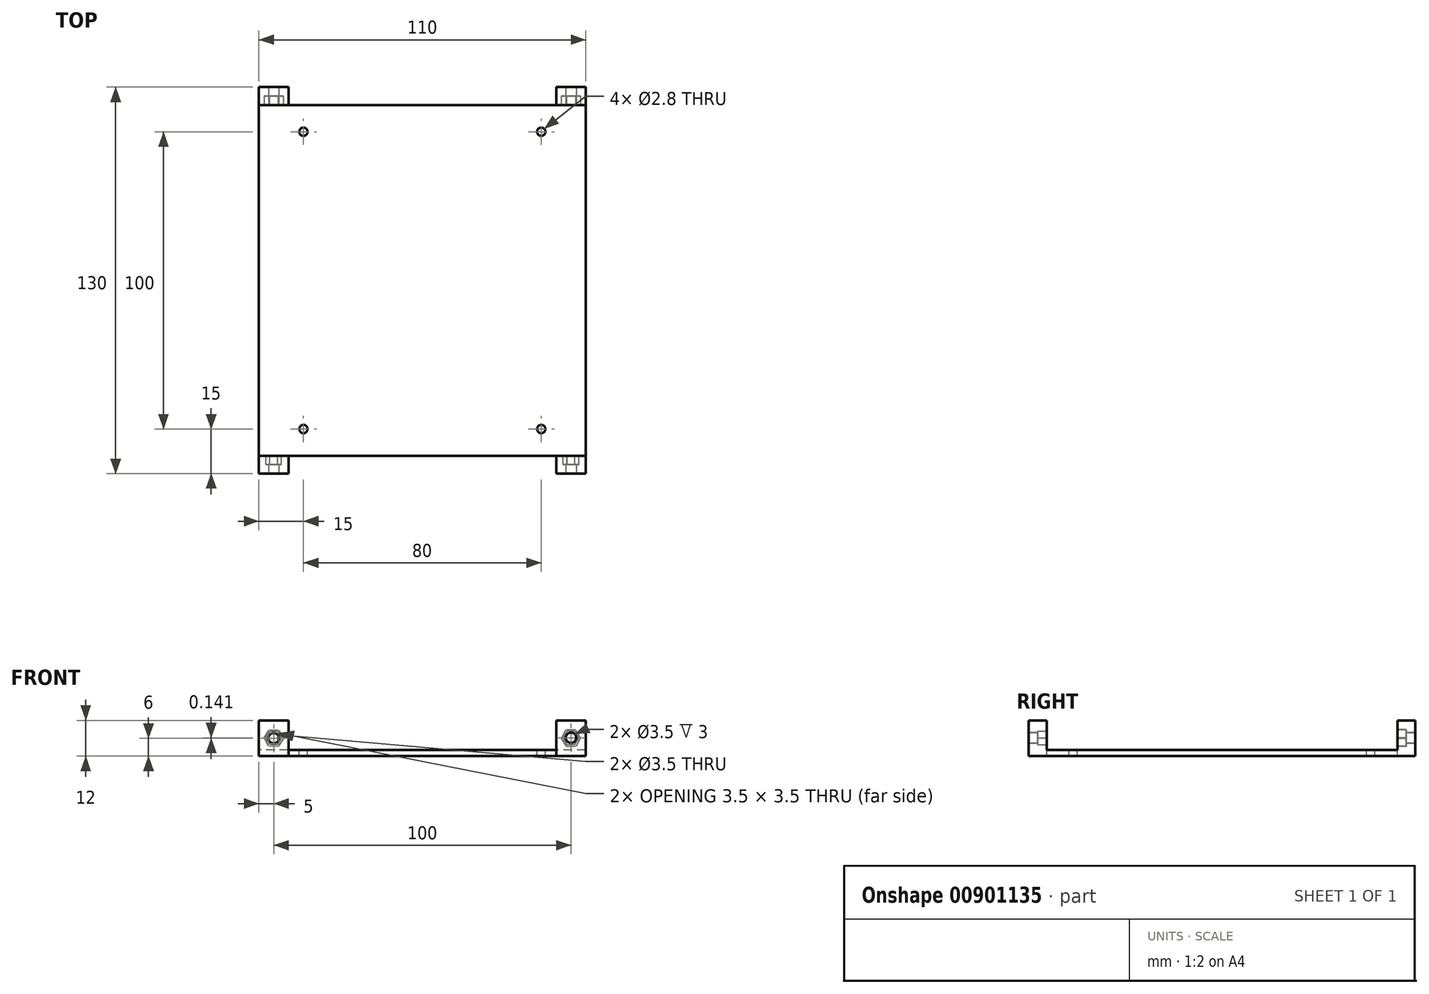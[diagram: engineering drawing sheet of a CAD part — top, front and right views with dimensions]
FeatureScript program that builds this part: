
annotation { "Feature Type Name" : "Feature", "Feature Type Description" : "" }
export const myFeature = defineFeature(function(context is Context, id is Id, definition is map)
    precondition{}
    {
        {
            var Q0;
            Q0=qCreatedBy(makeId("Right.planeOp"),FACE);
            var sketch = newSketch(context, id + "F0", { "sketchPlane" : qUnion([Q0])});
            skLineSegment(sketch, "E0.bottom", {"start": v(0, 25.4) * mm, "end": v(-59, 25.4) * mm});
            skLineSegment(sketch, "E0.top", {"start": v(0, 23.4) * mm, "end": v(-65, 23.4) * mm});
            skPoint(sketch, "E0.middle", {"position": v(0, 0) * mm});
            skLineSegment(sketch, "E1.top", {"start": v(-65, 35.4) * mm, "end": v(-59, 35.4) * mm});
            skLineSegment(sketch, "E1.right", {"start": v(-59, 25.4) * mm, "end": v(-59, 35.4) * mm});
            skLineSegment(sketch, "E2", {"start": v(0, 25.4) * mm, "end": v(0, 23.4) * mm, "construction": true});
            skLineSegment(sketch, "E3", {"start": v(-65, 35.4) * mm, "end": v(-65, 23.4) * mm});
            skLineSegment(sketch, "E4.MirrorCS", {"start": v(65, 35.4) * mm, "end": v(59, 35.4) * mm});
            skLineSegment(sketch, "E5.MirrorCS", {"start": v(0, 25.4) * mm, "end": v(59, 25.4) * mm});
            skLineSegment(sketch, "E6.MirrorCS", {"start": v(0, 23.4) * mm, "end": v(65, 23.4) * mm});
            skLineSegment(sketch, "E7.MirrorCS", {"start": v(59, 25.4) * mm, "end": v(59, 35.4) * mm});
            skLineSegment(sketch, "E8.MirrorCS", {"start": v(65, 35.4) * mm, "end": v(65, 23.4) * mm});
            skSolve(sketch);
        }
        {
            var Q0;
            Q0 = qSketchRegion(id + "F0", true);
            extrude(context, id + "F1", {"entities" : qUnion([Q0]), "endBound" : BoundingType.SYMMETRIC, "depth" : 110 * mm, "offsetDistance" : 25 * mm});
        }
        {
            var Q0;
            Q0=makeQuery(id+"F1.opExtrude","SWEPT_FACE",FACE,{"disambiguationData":[OSD([sQuery(id+"F0.wireOp",EDGE,"E4.MirrorCS")])]});
            var sketch = newSketch(context, id + "F2", { "sketchPlane" : qUnion([Q0])});
            skLineSegment(sketch, "E9.bottom", {"start": v(-45, 65) * mm, "end": v(45, 65) * mm});
            skLineSegment(sketch, "E9.top", {"start": v(-45, 59) * mm, "end": v(45, 59) * mm});
            skLineSegment(sketch, "E9.left", {"start": v(-45, 65) * mm, "end": v(-45, 59) * mm});
            skLineSegment(sketch, "E9.right", {"start": v(45, 65) * mm, "end": v(45, 59) * mm});
            skLineSegment(sketch, "E10.bottom", {"start": v(-45, -59) * mm, "end": v(45, -59) * mm});
            skLineSegment(sketch, "E10.top", {"start": v(-45, -65) * mm, "end": v(45, -65) * mm});
            skLineSegment(sketch, "E10.left", {"start": v(-45, -59) * mm, "end": v(-45, -65) * mm});
            skLineSegment(sketch, "E10.right", {"start": v(45, -59) * mm, "end": v(45, -65) * mm});
            skLineSegment(sketch, "E11", {"start": v(0, 89.7) * mm, "end": v(0, -84.78) * mm, "construction": true});
            skSolve(sketch);
        }
        {
            var Q0;
            Q0 = qSketchRegion(id + "F2", true);
            extrude(context, id + "F3", {"entities" : qUnion([Q0]), "operationType" : NewBodyOperationType.REMOVE, "oppositeDirection" : true, "depth" : 25 * mm, "offsetDistance" : 25 * mm});
        }
        {
            var Q0;
            {var subQ1=sQuery(id+"F0.wireOp",EDGE,"E3");Q0=makeQuery(id+"F3.boolean.opBoolean","SPLIT",FACE,{"disambiguationData":[TD([makeQuery(id+"F3.opExtrude","SWEPT_FACE",FACE,{"disambiguationData":[OSD([sQuery(id+"F2.wireOp",EDGE,"E10.left")])]})])],"derivedFrom":makeQuery(id+"F1.opExtrude","SWEPT_FACE",FACE,{"disambiguationData":[OSD([subQ1])]})});}
            var sketch = newSketch(context, id + "F4", { "sketchPlane" : qUnion([Q0])});
            skCircle(sketch, "E12", {"center": v(-50, 29.4) * mm, "radius": 1.75 * mm});
            skPoint(sketch, "E12.centerSnap0", {"position": v(-55, 29.4) * mm});
            skCircle(sketch, "E13", {"center": v(50, 29.54) * mm, "radius": 1.75 * mm});
            skLineSegment(sketch, "E14", {"start": v(-55, 29.4) * mm, "end": v(54.87, 29.4) * mm, "construction": true});
            skSolve(sketch);
        }
        {
            var Q0;
            Q0 = qSketchRegion(id + "F4", true);
            extrude(context, id + "F5", {"entities" : qUnion([Q0]), "operationType" : NewBodyOperationType.REMOVE, "endBound" : BoundingType.THROUGH_ALL, "oppositeDirection" : true, "depth" : 25 * mm, "offsetDistance" : 25 * mm});
        }
        {
            var Q0;
            {var subQ3=sQuery(id+"F0.wireOp",EDGE,"E7.MirrorCS");Q0=makeQuery(id+"F3.boolean.opBoolean","SPLIT",FACE,{"disambiguationData":[TD([makeQuery(id+"F3.opExtrude","SWEPT_FACE",FACE,{"disambiguationData":[OSD([sQuery(id+"F2.wireOp",EDGE,"E9.left")])]})])],"derivedFrom":makeQuery(id+"F1.opExtrude","SWEPT_FACE",FACE,{"disambiguationData":[OSD([subQ3])]})});}
            var sketch = newSketch(context, id + "F6", { "sketchPlane" : qUnion([Q0])});
            skCircle(sketch, "E15.cCircle", {"center": v(-50, 29.4) * mm, "radius": 2.8 * mm, "construction": true});
            skLineSegment(sketch, "E15.0", {"start": v(-48.27, 32.13) * mm, "end": v(-46.77, 29.27) * mm});
            skLineSegment(sketch, "E15.1", {"start": v(-46.77, 29.27) * mm, "end": v(-48.5, 26.54) * mm});
            skLineSegment(sketch, "E15.2", {"start": v(-48.5, 26.54) * mm, "end": v(-51.73, 26.67) * mm});
            skLineSegment(sketch, "E15.3", {"start": v(-51.73, 26.67) * mm, "end": v(-53.23, 29.53) * mm});
            skLineSegment(sketch, "E15.4", {"start": v(-53.23, 29.53) * mm, "end": v(-51.5, 32.26) * mm});
            skLineSegment(sketch, "E15.5", {"start": v(-51.5, 32.26) * mm, "end": v(-48.27, 32.13) * mm});
            skPoint(sketch, "E15.0.midPoint", {"position": v(-47.52, 30.7) * mm});
            skLineSegment(sketch, "E16", {"start": v(0, 29.86) * mm, "end": v(0, -10.04) * mm, "construction": true});
            skLineSegment(sketch, "E17.MirrorCS", {"start": v(53.23, 29.53) * mm, "end": v(51.5, 32.26) * mm});
            skLineSegment(sketch, "E18.MirrorCS", {"start": v(48.27, 32.13) * mm, "end": v(46.77, 29.27) * mm});
            skLineSegment(sketch, "E19.MirrorCS", {"start": v(51.5, 32.26) * mm, "end": v(48.27, 32.13) * mm});
            skCircle(sketch, "E20.MirrorC", {"center": v(50, 29.4) * mm, "radius": 2.8 * mm, "construction": true});
            skLineSegment(sketch, "E21.MirrorCS", {"start": v(51.73, 26.67) * mm, "end": v(53.23, 29.53) * mm});
            skLineSegment(sketch, "E22.MirrorCS", {"start": v(48.5, 26.54) * mm, "end": v(51.73, 26.67) * mm});
            skLineSegment(sketch, "E23.MirrorCS", {"start": v(46.77, 29.27) * mm, "end": v(48.5, 26.54) * mm});
            skPoint(sketch, "E24.MirrorP", {"position": v(47.52, 30.7) * mm});
            skSolve(sketch);
        }
        {
            var Q0;
            Q0 = qSketchRegion(id + "F6", true);
            extrude(context, id + "F7", {"entities" : qUnion([Q0]), "operationType" : NewBodyOperationType.REMOVE, "oppositeDirection" : true, "depth" : 3 * mm, "offsetDistance" : 25 * mm});
        }
        {
            var Q0;
            {var subQ3=sQuery(id+"F0.wireOp",EDGE,"E1.right");Q0=makeQuery(id+"F3.boolean.opBoolean","SPLIT",FACE,{"disambiguationData":[TD([makeQuery(id+"F3.opExtrude","SWEPT_FACE",FACE,{"disambiguationData":[OSD([sQuery(id+"F2.wireOp",EDGE,"E10.right")])]})])],"derivedFrom":makeQuery(id+"F1.opExtrude","SWEPT_FACE",FACE,{"disambiguationData":[OSD([subQ3])]})});}
            var sketch = newSketch(context, id + "F8", { "sketchPlane" : qUnion([Q0])});
            skCircle(sketch, "E25.cCircle", {"center": v(-50, 29.54) * mm, "radius": 2.3 * mm, "construction": true});
            skLineSegment(sketch, "E25.0", {"start": v(-48.69, 31.85) * mm, "end": v(-47.34, 29.56) * mm});
            skLineSegment(sketch, "E25.1", {"start": v(-47.34, 29.56) * mm, "end": v(-48.66, 27.25) * mm});
            skLineSegment(sketch, "E25.2", {"start": v(-48.66, 27.25) * mm, "end": v(-51.31, 27.23) * mm});
            skLineSegment(sketch, "E25.3", {"start": v(-51.31, 27.23) * mm, "end": v(-52.66, 29.52) * mm});
            skLineSegment(sketch, "E25.4", {"start": v(-52.66, 29.52) * mm, "end": v(-51.34, 31.83) * mm});
            skLineSegment(sketch, "E25.5", {"start": v(-51.34, 31.83) * mm, "end": v(-48.69, 31.85) * mm});
            skPoint(sketch, "E25.0.midPoint", {"position": v(-48.02, 30.7) * mm});
            skLineSegment(sketch, "E26", {"start": v(0, 43.64) * mm, "end": v(0, -10.98) * mm, "construction": true});
            skLineSegment(sketch, "E27.MirrorCS", {"start": v(48.69, 31.85) * mm, "end": v(47.34, 29.56) * mm});
            skLineSegment(sketch, "E28.MirrorCS", {"start": v(48.66, 27.25) * mm, "end": v(51.31, 27.23) * mm});
            skLineSegment(sketch, "E29.MirrorCS", {"start": v(51.34, 31.83) * mm, "end": v(48.69, 31.85) * mm});
            skCircle(sketch, "E30.MirrorC", {"center": v(50, 29.54) * mm, "radius": 2.3 * mm, "construction": true});
            skLineSegment(sketch, "E31.MirrorCS", {"start": v(47.34, 29.56) * mm, "end": v(48.66, 27.25) * mm});
            skLineSegment(sketch, "E32.MirrorCS", {"start": v(52.66, 29.52) * mm, "end": v(51.34, 31.83) * mm});
            skLineSegment(sketch, "E33.MirrorCS", {"start": v(51.31, 27.23) * mm, "end": v(52.66, 29.52) * mm});
            skPoint(sketch, "E34.MirrorP", {"position": v(48.02, 30.7) * mm});
            skSolve(sketch);
        }
        {
            var Q0;
            Q0 = qSketchRegion(id + "F8", true);
            extrude(context, id + "F9", {"entities" : qUnion([Q0]), "operationType" : NewBodyOperationType.REMOVE, "oppositeDirection" : true, "depth" : 3 * mm, "offsetDistance" : 25 * mm});
        }
        {
            var Q0;
            Q0=makeQuery(id+"F1.opExtrude","SWEPT_FACE",FACE,{"disambiguationData":[OSD([sQuery(id+"F0.wireOp",EDGE,"E0.bottom"),sQuery(id+"F0.wireOp",EDGE,"E5.MirrorCS")])]});
            var sketch = newSketch(context, id + "F10", { "sketchPlane" : qUnion([Q0])});
            skCircle(sketch, "E35", {"center": v(-40, 50) * mm, "radius": 1.4 * mm});
            skLineSegment(sketch, "E36", {"start": v(0, 59) * mm, "end": v(0, -59) * mm, "construction": true});
            skLineSegment(sketch, "E37", {"start": v(55, 0) * mm, "end": v(-55, 0) * mm, "construction": true});
            skCircle(sketch, "E38.MirrorC", {"center": v(40, 50) * mm, "radius": 1.4 * mm});
            skCircle(sketch, "E39.MirrorC", {"center": v(-40, -50) * mm, "radius": 1.4 * mm});
            skCircle(sketch, "E40.MirrorC", {"center": v(40, -50) * mm, "radius": 1.4 * mm});
            skLineSegment(sketch, "E41.MirrorCS", {"start": v(0, -59) * mm, "end": v(0, 59) * mm, "construction": true});
            skSolve(sketch);
        }
        {
            var Q0;
            Q0 = qSketchRegion(id + "F10", true);
            extrude(context, id + "F11", {"entities" : qUnion([Q0]), "operationType" : NewBodyOperationType.REMOVE, "oppositeDirection" : true, "depth" : 25 * mm, "offsetDistance" : 25 * mm});
        }
    });
